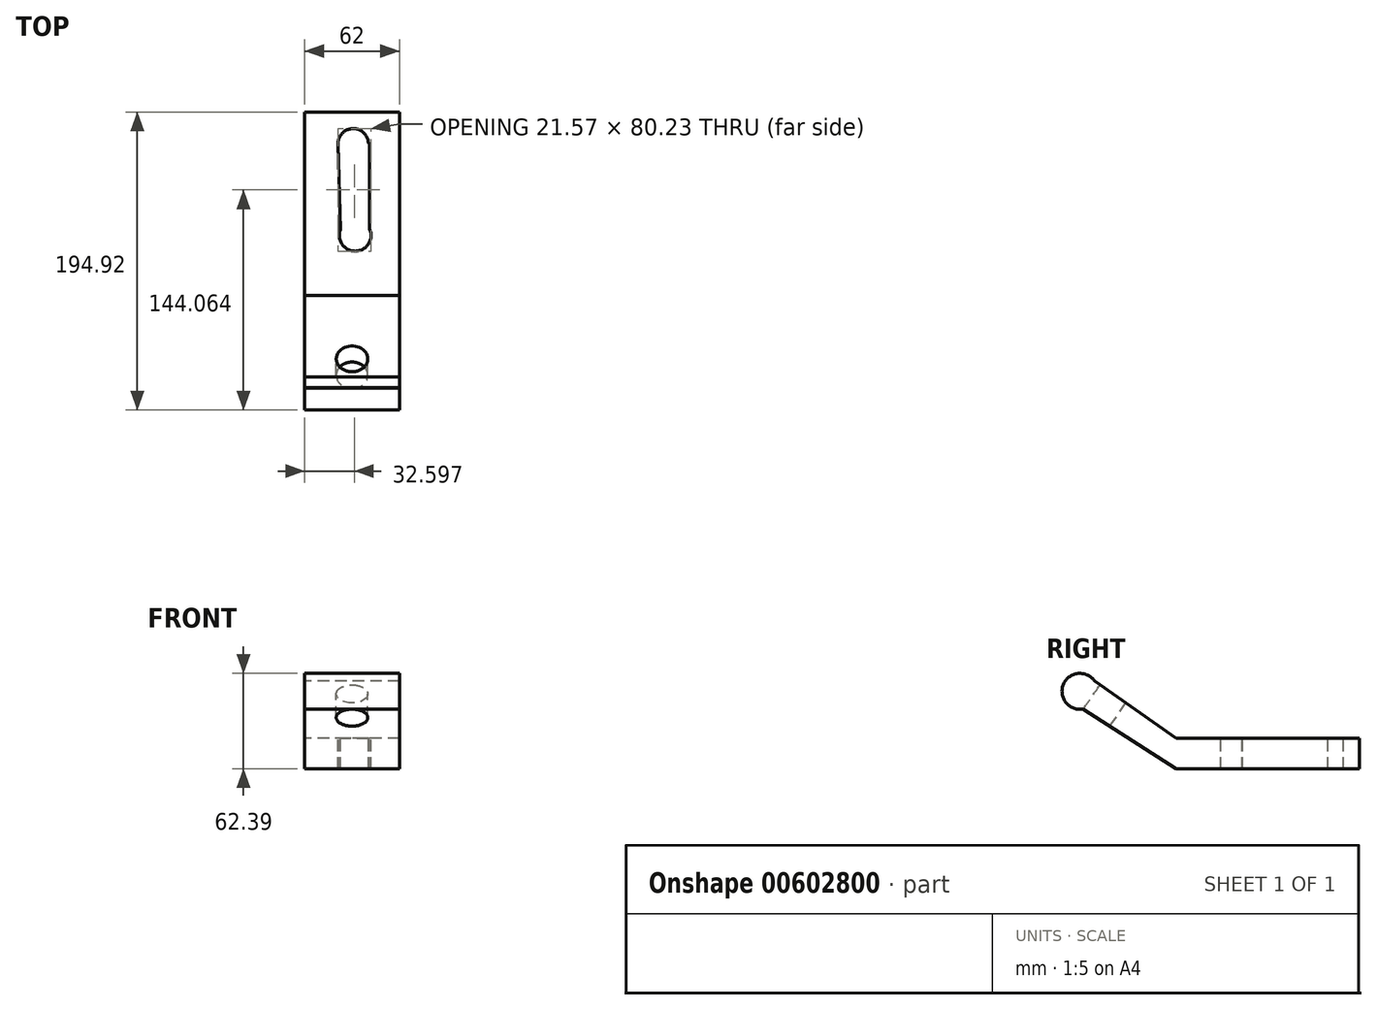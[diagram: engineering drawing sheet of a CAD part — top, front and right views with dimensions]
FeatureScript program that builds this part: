
annotation { "Feature Type Name" : "Feature", "Feature Type Description" : "" }
export const myFeature = defineFeature(function(context is Context, id is Id, definition is map)
    precondition{}
    {
        {
            var Q0;
            Q0=qCreatedBy(makeId("Right.planeOp"),FACE);
            var sketch = newSketch(context, id + "F0", { "sketchPlane" : qUnion([Q0])});
            skLineSegment(sketch, "E0.bottom", {"start": v(-47.97, 5.6) * mm, "end": v(72.03, 5.6) * mm});
            skLineSegment(sketch, "E0.top", {"start": v(-47.97, -14.4) * mm, "end": v(72.03, -14.4) * mm});
            skLineSegment(sketch, "E0.left", {"start": v(-47.97, 5.6) * mm, "end": v(-47.97, -14.4) * mm});
            skLineSegment(sketch, "E0.right", {"start": v(72.03, 5.6) * mm, "end": v(72.03, -14.4) * mm});
            skLineSegment(sketch, "E1", {"start": v(72.03, -4.4) * mm, "end": v(62.03, -4.4) * mm});
            skLineSegment(sketch, "E2", {"start": v(-47.97, 5.6) * mm, "end": v(-108.68, 47.91) * mm});
            skLineSegment(sketch, "E3", {"start": v(-108.68, 47.91) * mm, "end": v(-116.94, 29.7) * mm});
            skLineSegment(sketch, "E4", {"start": v(-116.94, 29.7) * mm, "end": v(-47.97, -14.4) * mm});
            skSolve(sketch);
        }
        {
            var Q0;
            Q0 = qSketchRegion(id + "F0", true);
            extrude(context, id + "F1", {"entities" : qUnion([Q0]), "depth" : 62 * mm, "offsetDistance" : 25 * mm});
        }
        {
            var Q0;
            Q0=qCreatedBy(makeId("Right.planeOp"),FACE);
            var sketch = newSketch(context, id + "F2", { "sketchPlane" : qUnion([Q0])});
            skCircle(sketch, "E5", {"center": v(-111.14, 36.24) * mm, "radius": 11.75 * mm});
            skSolve(sketch);
        }
        {
            var Q0;
            Q0 = qSketchRegion(id + "F2", true);
            extrude(context, id + "F3", {"entities" : qUnion([Q0]), "operationType" : NewBodyOperationType.ADD, "depth" : 62 * mm, "offsetDistance" : 25 * mm});
        }
        {
            var Q0;
            Q0=makeQuery(id+"F1.opExtrude","SWEPT_FACE",FACE,{"disambiguationData":[OSD([sQuery(id+"F0.wireOp",EDGE,"E0.bottom")])]});
            var sketch = newSketch(context, id + "F4", { "sketchPlane" : qUnion([Q0])});
            skLineSegment(sketch, "E6", {"start": v(31.78, 51.32) * mm, "end": v(42.61, 51.32) * mm});
            skCircle(sketch, "E7", {"center": v(31.78, 51.32) * mm, "radius": 9.97 * mm});
            skLineSegment(sketch, "E8", {"start": v(42.61, 51.32) * mm, "end": v(42.61, -8.57) * mm});
            skLineSegment(sketch, "E9", {"start": v(42.61, -8.57) * mm, "end": v(23.5, -8.57) * mm});
            skLineSegment(sketch, "E10", {"start": v(23.5, -8.57) * mm, "end": v(21.81, 51.03) * mm});
            skCircle(sketch, "E11", {"center": v(33.05, -8.57) * mm, "radius": 10.37 * mm});
            skSolve(sketch);
        }
        {
            var Q0;
            Q0 = qSketchRegion(id + "F4", true);
            extrude(context, id + "F5", {"entities" : qUnion([Q0]), "operationType" : NewBodyOperationType.REMOVE, "oppositeDirection" : true, "depth" : 62 * mm, "offsetDistance" : 25 * mm});
        }
        {
            var Q0;
            {var subQ3=sQuery(id+"F0.wireOp",EDGE,"E2");var subQ6=sQuery(id+"F0.wireOp",EDGE,"E0.bottom");Q0=makeQuery(id+"F3.boolean.opBoolean","SPLIT",FACE,{"disambiguationData":[TD([makeQuery(id+"F1.opExtrude","SWEPT_FACE",FACE,{"disambiguationData":[OSD([subQ6])]})])],"derivedFrom":makeQuery(id+"F1.opExtrude","SWEPT_FACE",FACE,{"disambiguationData":[OSD([subQ3])]})});}
            var sketch = newSketch(context, id + "F6", { "sketchPlane" : qUnion([Q0])});
            skCircle(sketch, "E12", {"center": v(31, -93.12) * mm, "radius": 10.33 * mm});
            skPoint(sketch, "E12.centerSnap0", {"position": v(31, -107.74) * mm});
            skSolve(sketch);
        }
        {
            var Q0;
            Q0 = qSketchRegion(id + "F6", true);
            extrude(context, id + "F7", {"entities" : qUnion([Q0]), "operationType" : NewBodyOperationType.REMOVE, "oppositeDirection" : true, "depth" : 62 * mm, "offsetDistance" : 25 * mm});
        }
    });
